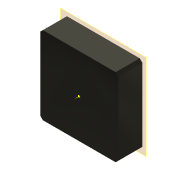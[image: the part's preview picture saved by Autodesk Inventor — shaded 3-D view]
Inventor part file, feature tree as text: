
AUTODESK INVENTOR PART (.ipt)
format: ipt  version: 2022 (Build 260153000, 153)  size: 152,064 bytes
history: native  units: mm
features: sketch x5, extrude x4, other x4, pattern_circular x2, projected_geometry x2, plane x1, reference x1
ambient origin geometry x8: Origin, YZ Plane, XZ Plane, XY Plane, X Axis, Y Axis, Z Axis, Center Point
bodies: Solid1 (feature_tree)
feature tree (19):
  plane  "Work Plane1"
  extrude  "Extrusion1"  Depth=14.0mm TaperAngle=0.0deg
  sketch  "Sketch2"  dims[d4=3.0mm d5=14.0mm d6=0.0mm]
  extrude  "Extrusion2"  Depth=14.0mm TaperAngle=0.0deg
  extrude  "Extrusion3"  Depth=3.0mm
  other  "Work Axis1"
  pattern_circular  "Circular Pattern1"  [2 undecoded]
  extrude  "Extrusion4"  Depth=6.0mm
  pattern_circular  "Circular Pattern2"  [2 undecoded]
  sketch  "Sketch1"  dims[d0=18.5mm d1=0.0mm d2=14.0mm d3=0.0mm]
  reference  "Reference1"
  sketch  "Sketch3"  dims[d7=20.0mm d8=90.0deg d10=3.0mm]
  projected_geometry  "Projected Loop1"
  sketch  "Sketch4"  dims[d11=6.0mm]
  projected_geometry  "Projected Loop2"
  sketch  "Sketch5"  dims[d12=15.0mm d13=4.0mm d14=6.0mm d15=15.0mm d16=18.5mm d17=0.0mm d18=40.0mm d19=360.0deg]
  other  "00_XY_stage-CHUO_SEIKI_LD-647-R1.iam"
  other  "00_XY_stage-CHUO_SEIKI_LD-647-R1-Top:1"
  other  "Assembly2"
note: 4 required parameter values undecoded (feature->parameter linkage not recoverable at this tier; creation-order binding heuristic only, values carry confidence <= 0.55)
